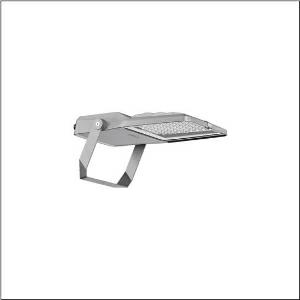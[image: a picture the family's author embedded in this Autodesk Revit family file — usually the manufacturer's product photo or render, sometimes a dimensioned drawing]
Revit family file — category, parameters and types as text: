
# Revit family: floodlight_fl_21_mini___pl43_5xa7773c2a1a_a3ea
name_source: partatom
category: Lighting Fixtures
units: mm (PartAtom-declared; Revit-internal decimal feet)

## family parameters
Cut with Voids When Loaded = No
Host = Face
Light Source = No
Part Type = Normal
Room Calculation Point = No
Round Connector Dimension = Use Diameter
Shared = No

## types (1)
- --- (1 x LED, 20010 lm, 163.5 W, 3000K)
    Apparent Load = 163 VA
    CIE Flux Codes = 27 78 99 100 100
    Color Rendering = 70
    Color Temperature = 3000K
    Default Elevation = 1800 mm
    Description = Floodlight FL 21 mini, floodlight, primary light control with lens, of PMMA, primary optical cover: protective disc, of toughened safety glass, transparent, light distribution: PL43, light emission: direct distribution, installation type: surface-mounted, LED, High Power LED, rated luminous flux: 20.010lm, luminous efficacy: 122lm/W, light colour: 730, colour temperature: 3000K, control gear: ON/OFF Multilumen, control: Temp-Guard, with terminal, 6-pole, mains connection: 220..240V, AC, 50/60Hz, start of lifetime: 164W, luminaire housing, of diecast aluminium, powder-coated, Siteco® metallic grey (DB 702S), corrosivity category C5 mid according to DIN EN ISO 12944, suitable for swimming pools, chlorine-resistant, sealing non-destructively replaceable, mounting bracket, of steel, galvanised, powder-coated, Siteco® metallic grey (DB 702S), ON/OFF, protection rating (complete): IP66, insulation class (complete): insulation class I (protective earthing), certification: CE, ENEC, VDE, protection symbol: D, impact resistance: IK08, permissible operating ambient temperature: -40..+40°C, permissible operating ambient temperature for outdoor applications: -40..+50°C, standard: DIN EN 12944, LABS conformity tested according to VDMA 24364:2018-05, packaging unit: 1 piece

Light Distribution: PL43
    Height = 70 mm
    Lamp = 1 x LED
    Lamp Light Flux = 20010 lm
    Lamp Power = 163.5 W
    Lamp count = 1
    Length = 485 mm
    Luminous efficacy = 122 lm/W
    Manufacturer = Siteco
    ModVariant = No
    Model = 5XA7773C2A1A
    Number of Poles = 1
    OnlyDefault = Yes
    Power Factor = 1
    Product Name = Floodlight FL 21 mini | PL43
    Product group = floodlight | pylon annexe
    ProductGroupID = 6200
    Protection Class = Protection class I
    Protection Degree = IP 66
    RLX_Detail_Level = 1
    RLX_Emergency_Light_Flux = 0 lm
    RLX_Emergency_Type = 0
    RLX_Emergency_Type_DB = No
    RlxData = <blob elided: 94261 chars, md5=1df08e50>
    Socket = socket
    Standby Power = 0 W
    System Light Flux = 20010 lm
    System Power = 163 W
    Type Comments = factory setting: luminous flux: 100 % | (ON | - | - | - | - | - | - | -) | 825 mA
    Type Image = l_1006845.jpg
    URL = http://relux.com
    VarID = @adj_162378
    Voltage = 0 V
    Weight = 0.00 kg
    Width = 337 mm

## geometry (parser evidence)
native form markers: Blend x4, Sweep x14
no freeform markers — native parametric forms only
